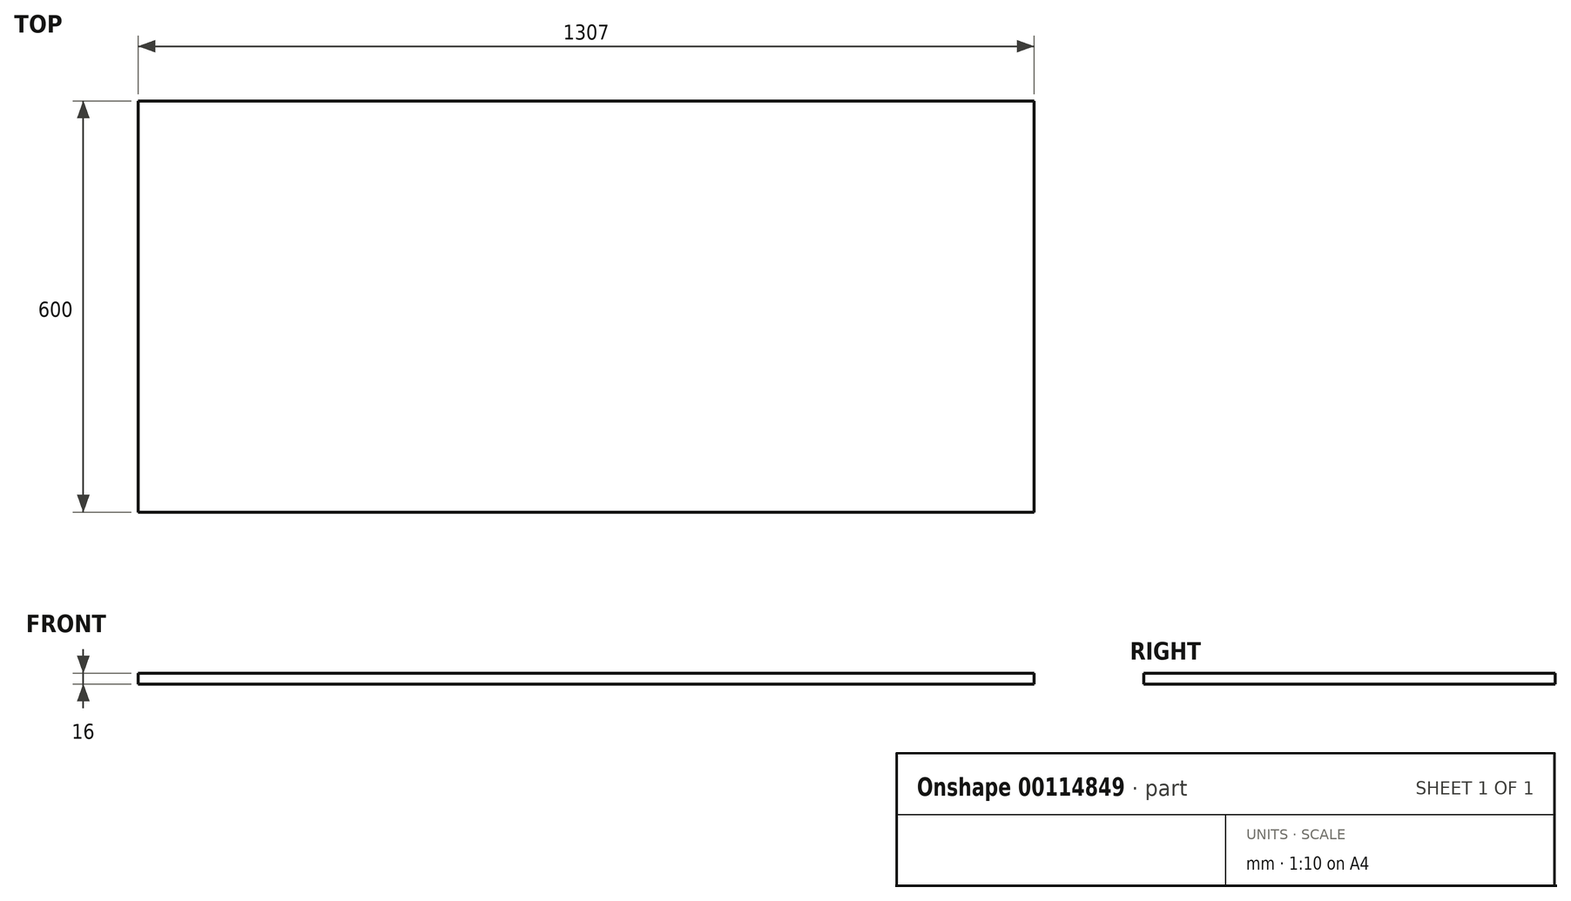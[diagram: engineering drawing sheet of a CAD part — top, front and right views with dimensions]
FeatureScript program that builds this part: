
annotation { "Feature Type Name" : "Feature", "Feature Type Description" : "" }
export const myFeature = defineFeature(function(context is Context, id is Id, definition is map)
    precondition{}
    {
        {
            var Q0;
            Q0=qCreatedBy(makeId("Top.planeOp"),FACE);
            var sketch = newSketch(context, id + "F0", { "sketchPlane" : qUnion([Q0])});
            skLineSegment(sketch, "E0.bottom", {"start": v(-653.5, 300) * mm, "end": v(653.5, 300) * mm});
            skLineSegment(sketch, "E0.top", {"start": v(-653.5, -300) * mm, "end": v(653.5, -300) * mm});
            skLineSegment(sketch, "E0.left", {"start": v(-653.5, 300) * mm, "end": v(-653.5, -300) * mm});
            skLineSegment(sketch, "E0.right", {"start": v(653.5, 300) * mm, "end": v(653.5, -300) * mm});
            skPoint(sketch, "E0.middle", {"position": v(0, 0) * mm});
            skSolve(sketch);
        }
        {
            var Q0;
            Q0=makeQuery(id+"F0.imprint","IMPRINT",FACE,{"disambiguationData":[TD([[makeQuery(id+"F0.imprint","IMPRINT",EDGE,{"derivedFrom":sQuery(id+"F0.wireOp",EDGE,"E0.bottom")}),-1.0]])]});
            extrude(context, id + "F1", {"entities" : qUnion([Q0]), "endBound" : BoundingType.SYMMETRIC, "depth" : 16 * mm});
        }
    });
